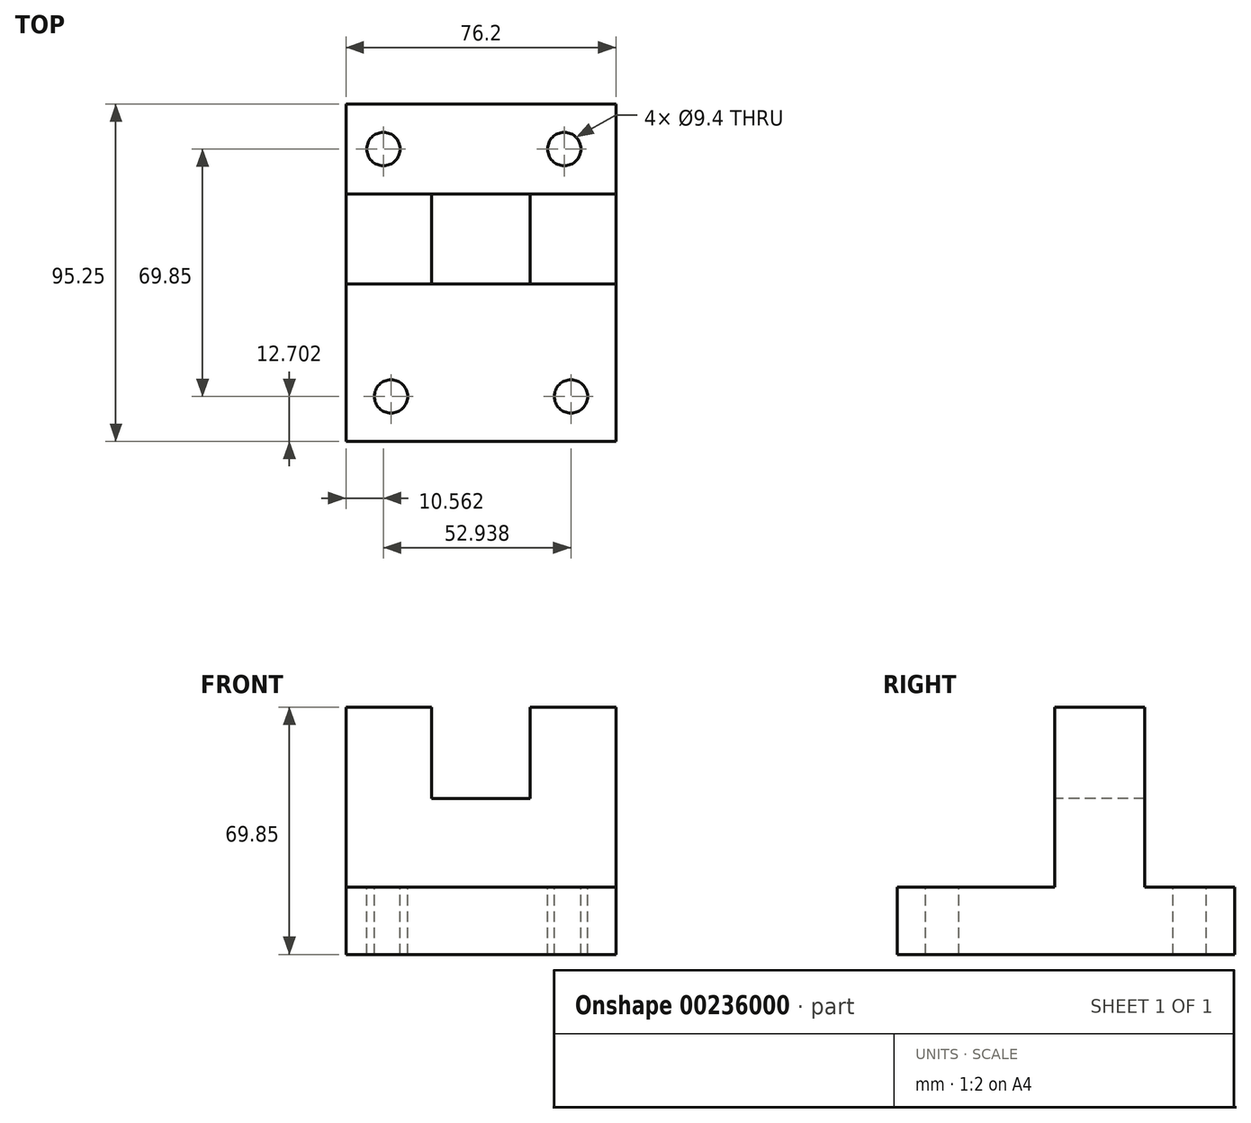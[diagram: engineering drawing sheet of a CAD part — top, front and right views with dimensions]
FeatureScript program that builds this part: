
annotation { "Feature Type Name" : "Feature", "Feature Type Description" : "" }
export const myFeature = defineFeature(function(context is Context, id is Id, definition is map)
    precondition{}
    {
        {
            var Q0;
            Q0=qCreatedBy(makeId("Right.planeOp"),FACE);
            var sketch = newSketch(context, id + "F0", { "sketchPlane" : qUnion([Q0])});
            skLineSegment(sketch, "E0.bottom", {"start": v(-64.07, -25.54) * mm, "end": v(-19.62, -25.54) * mm});
            skLineSegment(sketch, "E0.top", {"start": v(-64.07, -44.6) * mm, "end": v(31.18, -44.6) * mm});
            skLineSegment(sketch, "E0.left", {"start": v(-64.07, -25.54) * mm, "end": v(-64.07, -44.6) * mm});
            skLineSegment(sketch, "E0.right", {"start": v(31.18, -25.54) * mm, "end": v(31.18, -44.6) * mm});
            skLineSegment(sketch, "E1.top", {"start": v(5.78, 25.26) * mm, "end": v(-19.62, 25.26) * mm});
            skLineSegment(sketch, "E1.left", {"start": v(5.78, -25.54) * mm, "end": v(5.78, 25.26) * mm});
            skLineSegment(sketch, "E1.right", {"start": v(-19.62, -25.54) * mm, "end": v(-19.62, 25.26) * mm});
            skLineSegment(sketch, "E2.trimOffspring", {"start": v(5.78, -25.54) * mm, "end": v(31.18, -25.54) * mm});
            skSolve(sketch);
        }
        {
            var Q0;
            Q0 = qSketchRegion(id + "F0", true);
            extrude(context, id + "F1", {"entities" : qUnion([Q0]), "depth" : 76.2 * mm});
        }
        {
            var Q0;
            Q0=makeQuery(id+"F1.opExtrude","SWEPT_FACE",FACE,{"disambiguationData":[OSD([sQuery(id+"F0.wireOp",EDGE,"E1.right")])]});
            var sketch = newSketch(context, id + "F2", { "sketchPlane" : qUnion([Q0])});
            skLineSegment(sketch, "E3.bottom", {"start": v(24.18, 51.1) * mm, "end": v(52.02, 51.1) * mm});
            skLineSegment(sketch, "E3.top", {"start": v(24.18, -0.58) * mm, "end": v(52.02, -0.58) * mm});
            skLineSegment(sketch, "E3.left", {"start": v(24.18, 51.1) * mm, "end": v(24.18, -0.58) * mm});
            skLineSegment(sketch, "E3.right", {"start": v(52.02, 51.1) * mm, "end": v(52.02, -0.58) * mm});
            skPoint(sketch, "E3.middle", {"position": v(38.1, 25.26) * mm});
            skSolve(sketch);
        }
        {
            var Q0;
            Q0 = qSketchRegion(id + "F2", true);
            extrude(context, id + "F3", {"entities" : qUnion([Q0]), "operationType" : NewBodyOperationType.REMOVE, "endBound" : BoundingType.THROUGH_ALL, "oppositeDirection" : true, "depth" : 76.2 * mm});
        }
        {
            var Q0;
            Q0=makeQuery(id+"F1.opExtrude","SWEPT_FACE",FACE,{"disambiguationData":[OSD([sQuery(id+"F0.wireOp",EDGE,"E0.bottom")])]});
            var sketch = newSketch(context, id + "F4", { "sketchPlane" : qUnion([Q0])});
            skCircle(sketch, "E4", {"center": v(12.7, -51.37) * mm, "radius": 4.7 * mm});
            skCircle(sketch, "E5.MirrorC", {"center": v(63.5, -51.37) * mm, "radius": 4.7 * mm});
            skCircle(sketch, "E6", {"center": v(10.56, 18.48) * mm, "radius": 4.7 * mm});
            skCircle(sketch, "E7.MirrorC", {"center": v(61.6, 18.48) * mm, "radius": 4.7 * mm});
            skSolve(sketch);
        }
        {
            var Q0;
            Q0 = qSketchRegion(id + "F4", true);
            extrude(context, id + "F5", {"entities" : qUnion([Q0]), "operationType" : NewBodyOperationType.REMOVE, "depth" : 76.2 * mm});
        }
        {
            var Q0;
            Q0 = qSketchRegion(id + "F4", true);
            extrude(context, id + "F6", {"entities" : qUnion([Q0]), "operationType" : NewBodyOperationType.REMOVE, "endBound" : BoundingType.THROUGH_ALL, "oppositeDirection" : true, "depth" : 25.4 * mm});
        }
    });
